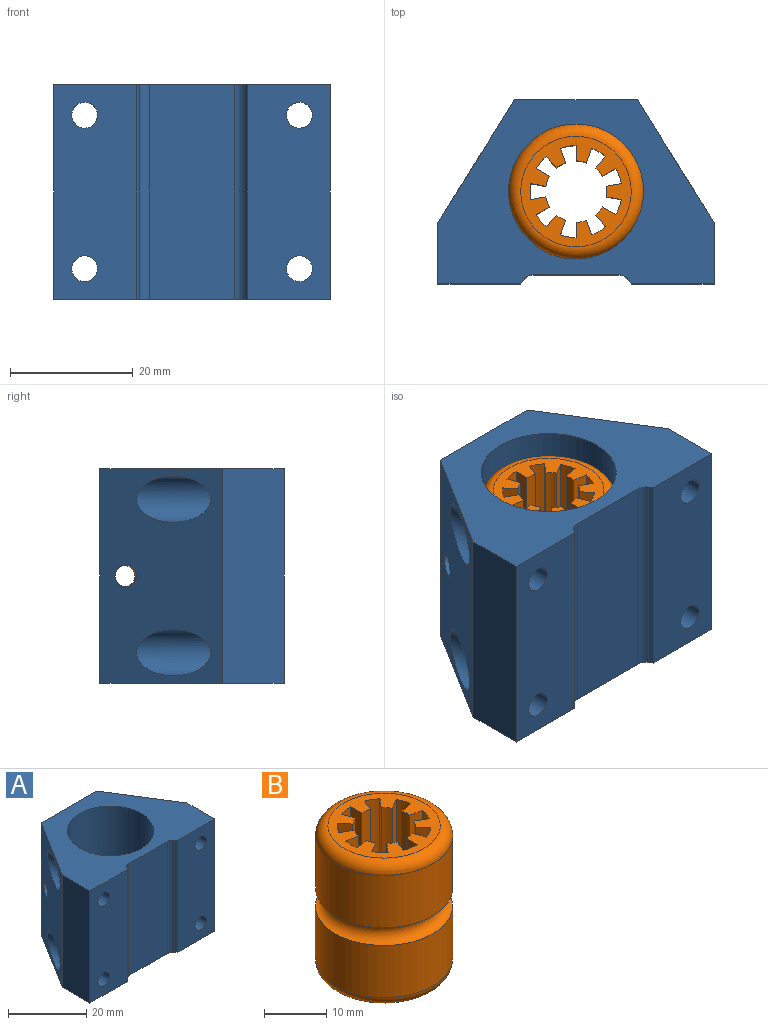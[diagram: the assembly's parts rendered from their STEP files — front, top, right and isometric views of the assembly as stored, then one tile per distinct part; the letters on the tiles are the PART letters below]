
ASSEMBLY  parts=2 mates=1
PART A: 28 faces, bbox 45.5x30.5x35.5 mm
  f0: plane 35x13.47mm, normal (0,-1,0), area 443.8mm2, adj f1,f4,f9,f19,f20,f23
  f1: plane 45x30mm, normal (0,0,1), area 694.7mm2, adj f0,f2,f3,f4,f5,f6,f7,f8
  f2: plane 35x10mm, normal (-1,0,0), area 350mm2, adj f1,f3,f8,f9
  f3: plane 35x13.47mm, normal (0,-1,0), area 443.8mm2, adj f1,f2,f9,f18,f21,f22
  f4: plane 35x10mm, normal (1,0,0), area 350mm2, adj f0,f1,f5,f9
  f5: plane 35x20mm, normal (0.85,0.53,0), area 647.4mm2, adj f1,f4,f6,f9,f14,f16,f27
  f6: plane 35x20mm, normal (0,1,0), area 700mm2, adj f1,f5,f8,f9
  f7: cylinder r=11mm len=35mm, axis (0,0,-1), area 2386.3mm2, adj f1,f9,f27
  f8: plane 35.46x20.46mm, normal (-0.85,0.53,0), area 647.4mm2, adj f1,f2,f6,f9,f10,f12,f27
  f9: plane 45x30mm, normal (0,0,-1), area 694.7mm2, adj f0,f2,f3,f4,f5,f6,f7,f8
  f10: cylinder r=3.75mm len=14mm, axis (0,1,0), area 188.5mm2, adj f8,f11
  f11: plane 7.5x7.5mm, normal (0,1,0), area 30.3mm2, adj f10,f21
  f12: cylinder r=3.75mm len=14mm, axis (0,1,0), area 188.5mm2, adj f8,f13
  f13: plane 7.5x7.5mm, normal (0,1,0), area 30.3mm2, adj f12,f18
  f14: cylinder r=3.75mm len=14mm, axis (0,1,0), area 188.5mm2, adj f5,f15
  f15: plane 7.5x7.5mm, normal (0,1,0), area 30.3mm2, adj f14,f20
  f16: cylinder r=3.75mm len=14mm, axis (0,1,0), area 188.5mm2, adj f5,f17
  f17: plane 7.5x7.5mm, normal (0,1,0), area 30.3mm2, adj f16,f19
  f18: cylinder r=2.1mm len=10mm, axis (0,1,0), area 131.9mm2, adj f3,f13
  f19: cylinder r=2.1mm len=10mm, axis (0,1,0), area 131.9mm2, adj f0,f17
  f20: cylinder r=2.1mm len=10mm, axis (0,1,0), area 131.9mm2, adj f0,f15
  f21: cylinder r=2.1mm len=10mm, axis (0,1,0), area 131.9mm2, adj f3,f11
  f22: plane 35x0.63mm, normal (0.83,-0.56,0), area 26.5mm2, adj f1,f3,f9,f26
  f23: plane 35x0.63mm, normal (-0.83,-0.56,0), area 26.5mm2, adj f0,f1,f9,f24
  f24: cylinder r=2mm len=35mm, axis (0,0,1), area 68.1mm2, adj f1,f9,f23,f25
  f25: plane 35x13.9mm, normal (0,-1,0), area 486.5mm2, adj f1,f9,f24,f26
  f26: cylinder r=2mm len=35mm, axis (0,0,1), area 68.1mm2, adj f1,f9,f22,f25
  f27: cylinder r=1.75mm len=27.44mm, axis (1,0,0), area 221.8mm2, adj f5,f7,f8
PART B: 43 faces, bbox 26.5x26.5x28 mm
  f0: cylinder r=11mm len=22mm, axis (0,0,-1), area 708.4mm2, adj f41,f42
  f1: cylinder r=5mm len=28mm, axis (0,0,-1), area 48.9mm2, adj f2,f36,f38,f39
  f2: plane 28x2.17mm, normal (0.5,-0.87,0), area 70mm2, adj f1,f3,f38,f39
  f3: cylinder r=7.5mm len=28mm, axis (0,0,-1), area 73.3mm2, adj f2,f4,f38,f39
  f4: plane 28x2.46mm, normal (-0.17,0.98,0), area 70mm2, adj f3,f5,f38,f39
  f5: cylinder r=5mm len=28mm, axis (0,0,-1), area 48.9mm2, adj f4,f6,f38,f39
  f6: plane 28x2.46mm, normal (-0.17,-0.98,0), area 70mm2, adj f5,f7,f38,f39
  f7: cylinder r=7.5mm len=28mm, axis (0,0,-1), area 73.3mm2, adj f6,f8,f38,f39
  f8: plane 28x2.17mm, normal (0.5,0.87,0), area 70mm2, adj f7,f9,f38,f39
  f9: cylinder r=5mm len=28mm, axis (0,0,-1), area 48.9mm2, adj f8,f10,f38,f39
  f10: plane 28x1.92mm, normal (-0.77,-0.64,0), area 70mm2, adj f9,f11,f38,f39
  f11: cylinder r=7.5mm len=28mm, axis (0,0,-1), area 73.3mm2, adj f10,f12,f38,f39
  f12: plane 28x2.35mm, normal (0.94,0.34,0), area 70mm2, adj f11,f13,f38,f39
  f13: cylinder r=5mm len=28mm, axis (0,0,-1), area 48.9mm2, adj f12,f14,f38,f39
  f14: plane 28x2.5mm, normal (-1,0,0), area 70mm2, adj f13,f15,f38,f39
  f15: cylinder r=7.5mm len=28mm, axis (0,0,-1), area 73.3mm2, adj f14,f16,f38,f39
  f16: plane 28x2.35mm, normal (0.94,-0.34,0), area 70mm2, adj f15,f17,f38,f39
  f17: cylinder r=5mm len=28mm, axis (0,0,-1), area 48.9mm2, adj f16,f18,f38,f39
  f18: plane 28x1.92mm, normal (-0.77,0.64,0), area 70mm2, adj f17,f19,f38,f39
  f19: cylinder r=7.5mm len=28mm, axis (0,0,-1), area 73.3mm2, adj f18,f20,f38,f39
  f20: plane 28x2.17mm, normal (0.5,-0.87,0), area 70mm2, adj f19,f21,f38,f39
  f21: cylinder r=5mm len=28mm, axis (0,0,-1), area 48.9mm2, adj f20,f22,f38,f39
  f22: plane 28x2.46mm, normal (-0.17,0.98,0), area 70mm2, adj f21,f23,f38,f39
  f23: cylinder r=7.5mm len=28mm, axis (0,0,-1), area 73.3mm2, adj f22,f24,f38,f39
  f24: plane 28x2.46mm, normal (-0.17,-0.98,0), area 70mm2, adj f23,f25,f38,f39
  f25: cylinder r=5mm len=28mm, axis (0,0,-1), area 48.9mm2, adj f24,f26,f38,f39
  f26: plane 28x2.17mm, normal (0.5,0.87,0), area 70mm2, adj f25,f27,f38,f39
  f27: cylinder r=7.5mm len=28mm, axis (0,0,-1), area 73.3mm2, adj f26,f28,f38,f39
  f28: plane 28x1.92mm, normal (-0.77,-0.64,0), area 70mm2, adj f27,f29,f38,f39
  f29: cylinder r=5mm len=28mm, axis (0,0,-1), area 48.9mm2, adj f28,f30,f38,f39
  f30: plane 28x2.35mm, normal (0.94,0.34,0), area 70mm2, adj f29,f31,f38,f39
  f31: cylinder r=7.5mm len=28mm, axis (0,0,-1), area 73.3mm2, adj f30,f32,f38,f39
  f32: plane 28x2.5mm, normal (-1,0,0), area 70mm2, adj f31,f33,f38,f39
  f33: cylinder r=5mm len=28mm, axis (0,0,-1), area 48.9mm2, adj f32,f34,f38,f39
  f34: plane 28x2.35mm, normal (0.94,-0.34,0), area 70mm2, adj f33,f35,f38,f39
  f35: cylinder r=7.5mm len=28mm, axis (0,0,-1), area 73.3mm2, adj f34,f36,f38,f39
  f36: plane 28x1.92mm, normal (-0.77,0.64,0), area 70mm2, adj f1,f35,f38,f39
  f37: cylinder r=11mm len=22mm, axis (0,0,-1), area 708.4mm2, adj f40,f42
  f38: plane 18x18mm, normal (0,0,1), area 126.8mm2, adj f1,f2,f3,f4,f5,f6,f7,f8
  f39: plane 18x18mm, normal (0,0,-1), area 126.8mm2, adj f1,f2,f3,f4,f5,f6,f7,f8
  f40: torus R=9mm, axis (0,0,1), area 202.8mm2, adj f37,f39
  f41: torus R=9mm, axis (0,0,1), area 202.8mm2, adj f0,f38
  f42: torus R=11mm, axis (0,0,1), area 342mm2, adj f0,f37
PLACE A t=(-0.55,-0.78,0.2)mm
PLACE B t=(-0.55,-0.78,-0.34)mm
MATE slider B.f0 <-> A.f7  axis (0,0,1) through (-0.55,-0.78,29.66)mm
